# Revit family: York CB-ABB-YK - Horizontal Throw, Bulkhead Mounted Active Chilled Beam,Face Base, Revit 2015 R1.0
name_source: partatom
category: Mechanical Equipment
revit_build: Autodesk Revit 2015 (Build: 20160512_1515(x64)
units: mm (PartAtom-declared; Revit-internal decimal feet)

## types (1)
- CB-ABB-YK
    (0) Front and Back Supply = Yes
    (1) Front Supply = No
    (2) Back Supply = No
    0-No Insulation = Yes
    00-None = No
    2 Feet = Yes
    2 Pipe LHC = Yes
    26 White = Yes
    2P1C - 2 Pipe Coil = No
    3 Feet = No
    4 Feet = No
    4 Pipe LHC = Yes
    4" Dia. = Yes
    4P1C - 4 Pipe Coil = Yes
    5 Feet = No
    5" Dia. = No
    6 Feet = No
    6" Dia. = No
    8" Dia. = No
    84- Black Paint = No
    A = 24 7/8"
    A1 = 12 7/16"
    Air Inlet Front Adapter Visibility = No
    Angle = 90.00°
    B = 21"
    B1 = Yes
    B2 = No
    B3 = No
    B4 = No
    BC-Egg Crate Grille = No
    BL-Linear Bar Grille = No
    Box Width = 18 1/8"
    Bracket Distance = 1"
    Bracket Length = 4"
    C = 24 1/4"
    CP-Circular Perforation = No
    Chilled Water Connection Diameter = 1"
    Clearance Material = Clearance
    D = 3 7/8"
    Default Elevation = 0"
    Description = Concealed Bulkhead Mounted Active Chilled Beam
    Dia Of Hole = 3/16"
    Distance = 3"
    E = 6 1/4"
    H12 - SS Flex Hose - 12in = No
    H18 - SS Flex Hose - 18in = No
    H24 - SS FLex Hose - 24in = No
    Heating Water Connection Diameter = 1"
    L - Left Hand = Yes
    L - ½” EcoShield (Foil Face) = No
    L1-Louvered Grille,Single Deflection = Yes
    LV-Louvered Grille = Yes
    Linear Bar Grille(BL) = No
    Linear Bar Visibilty = No
    MPT - Male Pipe Thread = No
    Manufacturer = York
    Material = Galvanealed G90,20 GA Sheet Metal
    Max Flow = 0 CFM
    Min Flow = 0 CFM
    Model = CB-ABB-YK, 4 - Pipe Coil, Left Hand
    Mounting Bracket Visibility = Yes
    Neck Size = 10"
    Pipe Coil Material = Copper
    Pipe Distance X1 = 8"
    Pipe Distance X2 = 4"
    Pipe Distance X3 = 2"
    Pipe Distance X5 = 6"
    Pipe L = 2"
    Pipe Length = 14 7/16"
    Pipe R = 1/4"
    Pipe Rotation Angle = 180.00°
    Plate Support Height = 20"
    Plate Support Width = 14"
    Plate Width = 15"
    R - Right Hand = No
    SWT - Sweat = Yes
    Select a Finish = 1
    Select a Nominal Beam Length = 1
    Select a Return Grille = 4
    Select a Supply Grille = 1
    Select a Water-Coil Piping Connection Type = 1
    Select a Water-Coil Type = 2
    Select an Air Inlet Size = 1
    Select an Air Nozzle Configuration = 1
    Select the Plenum Liner (External) = 1
    Select the Water-Coil Connection Side = 1
    Series = Chilled Beam
    URL = http://www.york.com
    Version = 3
    Visibility Of Perforation Plate = No
    Visibilty Of Return Grille Type = Yes
    Water Connection Location Selection = 0
    X-Center Distance = 3/8"
    Y-Center Distance = 3/8"

## geometry (parser evidence)
native form markers: Blend x6, Sweep x17
no freeform markers — native parametric forms only
